# Revit family: FU_Lounge_Sandler_Jump 5-1
name_source: partatom
category: Furniture
units: mm (PartAtom-declared; Revit-internal decimal feet)

## family parameters
Always vertical = Yes
Cut with Voids When Loaded = No
OmniClass Number = 23.40.20.00
OmniClass Title = General Furniture and Specialties
Room Calculation Point = No
Shared = No
Work Plane-Based = No

## types (1)
- Jump 5.1
    Default Elevation = 0 mm  [stored 0 ft]
    Depth = 640 mm  [stored 2.09974 ft]
    Description = Lounge armchair, solid wood, curved semi-circular back which blends with the rear legs. Webbed seat with differentiated density padding for greater comfort, wraparound back upholstered in fabric and/or leather as well as the seat.
    Height = 785 mm
    Manufacturer = Sandler
    Model = Jump 5.1
    URL = https://www.sandlerseating.com
    Width = 595 mm  [stored 1.9521 ft]

note: [stored X ft] marks values corroborated as IEEE doubles in the binary element streams (Revit-internal decimal feet)

## geometry (parser evidence)
native form markers: Sweep x17
no freeform markers — native parametric forms only
